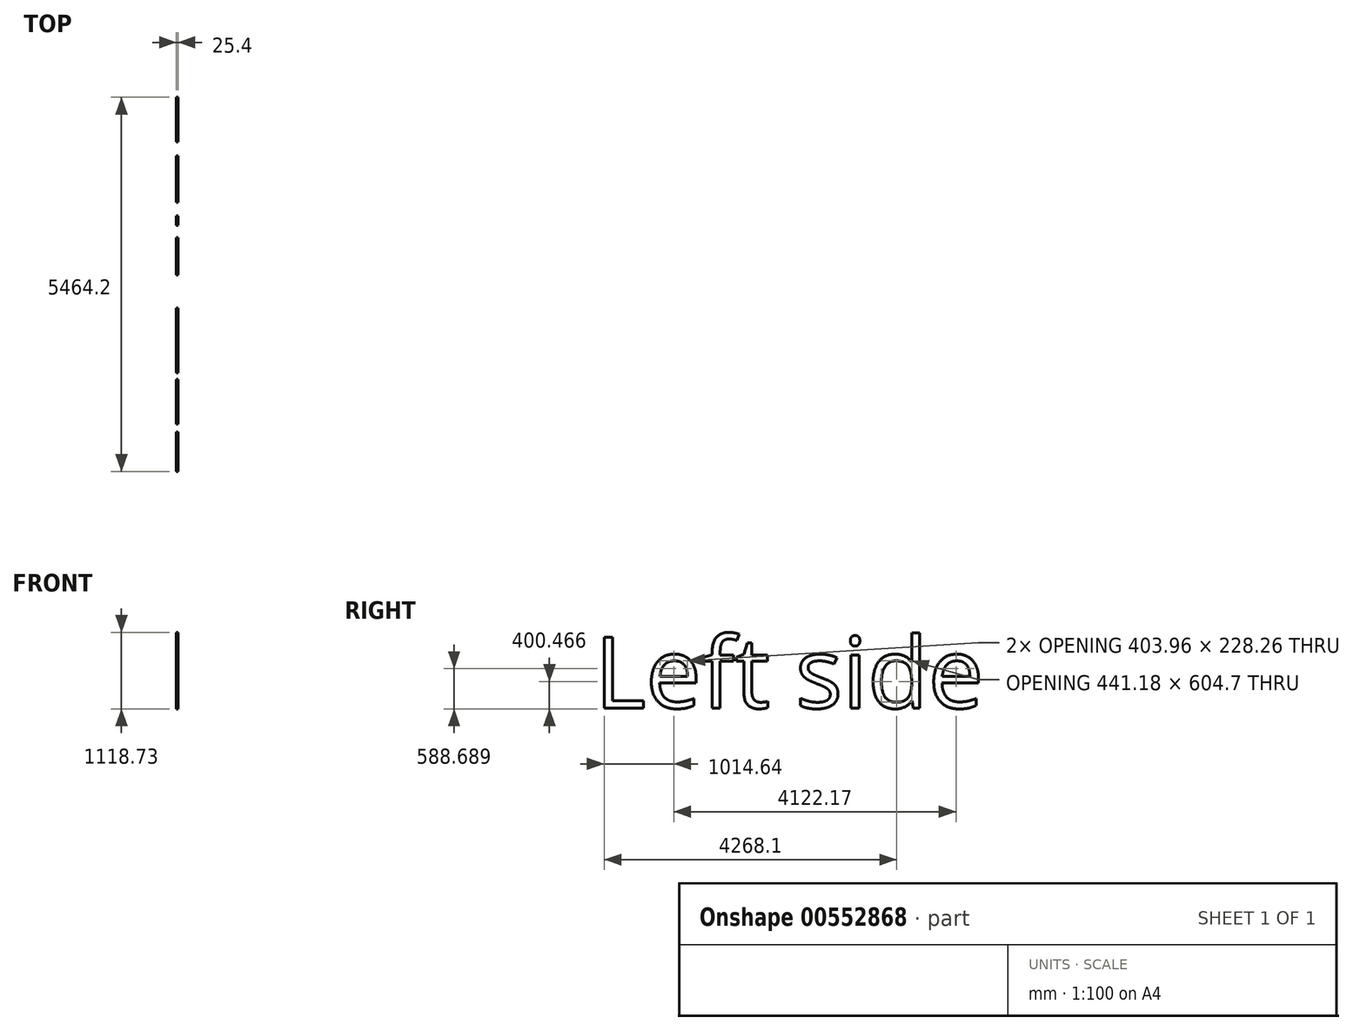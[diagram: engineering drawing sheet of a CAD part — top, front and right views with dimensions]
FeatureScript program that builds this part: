
annotation { "Feature Type Name" : "Feature", "Feature Type Description" : "" }
export const myFeature = defineFeature(function(context is Context, id is Id, definition is map)
    precondition{}
    {
        {
            var Q0;
            Q0=qCreatedBy(makeId("Front.planeOp"),FACE);
            var sketch = newSketch(context, id + "F0", { "sketchPlane" : qUnion([Q0])});
            skText(sketch, "E0", { "text": "some text here", "fontName": "OpenSans-Regular.ttf"});
            const initialGuessF0  = {"E0": [0.03316, 0.04265, 1, 0, 0.12526]};
            skSetInitialGuess(sketch, initialGuessF0);
            skSolve(sketch);
        }
        {
            var Q0;
            Q0 = qSketchRegion(id + "F0", true);
            var sketch = newSketch(context, id + "F1", { "sketchPlane" : qUnion([Q0])});
            skText(sketch, "E1", { "text": "more", "fontName": "OpenSans-Regular.ttf"});
            const initialGuessF1  = {"E1": [0.50737, -0.23907, 1, 0, 0.77419]};
            skSetInitialGuess(sketch, initialGuessF1);
            skSolve(sketch);
        }
        {
            var Q0;
            Q0=qCreatedBy(makeId("Right.planeOp"),FACE);
            var sketch = newSketch(context, id + "F2", { "sketchPlane" : qUnion([Q0])});
            skText(sketch, "E2", { "text": "Right side", "fontName": "OpenSans-Regular.ttf"});
            const initialGuessF2  = {"E2": [-0.45302, -0.07912, 1, 0, 0.27778]};
            skSetInitialGuess(sketch, initialGuessF2);
            skSolve(sketch);
        }
        {
            var Q0;
            Q0=makeQuery(id+"F2.imprint","IMPRINT",FACE,{"disambiguationData":[TD([[makeQuery(id+"F2.imprint","IMPRINT",EDGE,{"derivedFrom":sQuery(id+"F2.wireOp",EDGE,"E2.sketch_text.stroke-111")}),-1.0]])]});
            var sketch = newSketch(context, id + "F3", { "sketchPlane" : qUnion([Q0])});
            skText(sketch, "E3", { "text": "Left side", "fontName": "OpenSans-Regular.ttf"});
            const initialGuessF3  = {"E3": [-0.7265, -0.47585, 1, 0, 1.03934]};
            skSetInitialGuess(sketch, initialGuessF3);
            skSolve(sketch);
        }
        {
            var Q0;
            Q0 = qSketchRegion(id + "F3", true);
            extrude(context, id + "F4", {"entities" : qUnion([Q0]), "depth" : 25.4 * mm, "offsetDistance" : 25.4 * mm});
        }
    });
